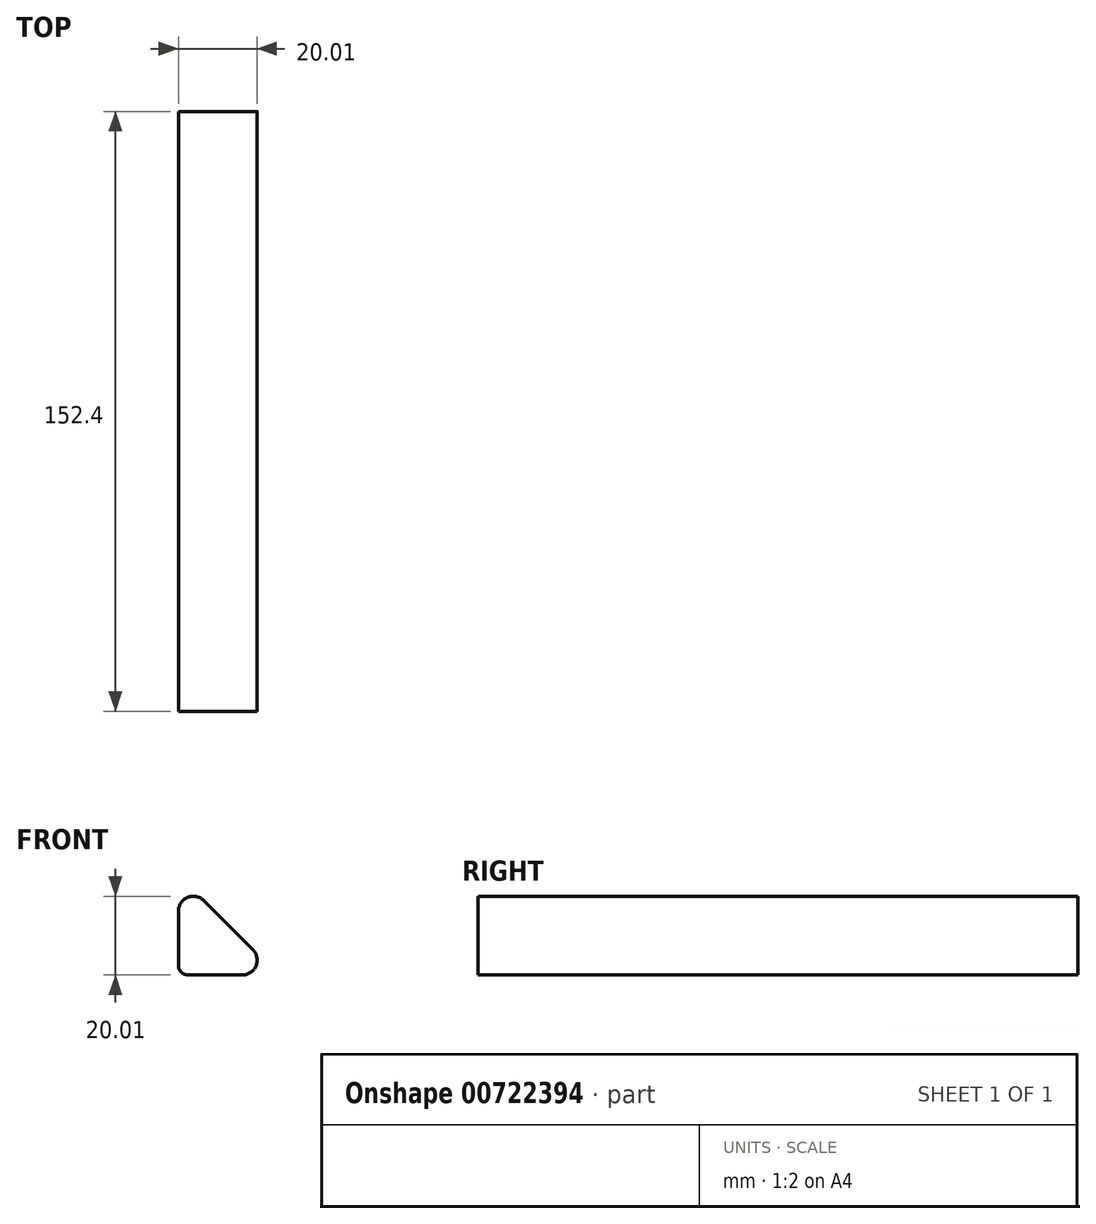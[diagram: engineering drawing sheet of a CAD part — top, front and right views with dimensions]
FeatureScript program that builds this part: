
annotation { "Feature Type Name" : "Feature", "Feature Type Description" : "" }
export const myFeature = defineFeature(function(context is Context, id is Id, definition is map)
    precondition{}
    {
        {
            var Q0;
            Q0=qCreatedBy(makeId("Front.planeOp"),FACE);
            var sketch = newSketch(context, id + "F0", { "sketchPlane" : qUnion([Q0])});
            skLineSegment(sketch, "E0", {"start": v(0, 0) * mm, "end": v(0, 25.4) * mm});
            skLineSegment(sketch, "E1", {"start": v(0, 25.4) * mm, "end": v(25.4, 0) * mm});
            skLineSegment(sketch, "E2", {"start": v(25.4, 0) * mm, "end": v(0, 0) * mm});
            skSolve(sketch);
        }
        {
            var Q0;
            Q0 = qSketchRegion(id + "F0", true);
            extrude(context, id + "F1", {"entities" : qUnion([Q0]), "depth" : 152.4 * mm, "offsetDistance" : 25.4 * mm});
        }
        {
            var Q0;
            Q0=makeQuery(id+"F1.opExtrude","SWEPT_EDGE",EDGE,{"disambiguationData":[OSD([sQuery(id+"F0.wireOp",EDGE,"E0"),sQuery(id+"F0.wireOp",EDGE,"E1")])]});
            var Q1;
            Q1=makeQuery(id+"F1.opExtrude","SWEPT_EDGE",EDGE,{"disambiguationData":[OSD([sQuery(id+"F0.wireOp",EDGE,"E1"),sQuery(id+"F0.wireOp",EDGE,"E2")])]});
            fillet(context, id + "F2", {"entities" : qUnion([Q0, Q1]), "radius" : 3.8 * mm, "tangentPropagation" : true, "allowEdgeOverflow" : false});
        }
        {
            var Q0;
            Q0=makeQuery(id+"F1.opExtrude","SWEPT_EDGE",EDGE,{"disambiguationData":[OSD([sQuery(id+"F0.wireOp",EDGE,"E0"),sQuery(id+"F0.wireOp",EDGE,"E2")])]});
            fillet(context, id + "F3", {"entities" : qUnion([Q0]), "radius" : 2.54 * mm, "tangentPropagation" : true, "allowEdgeOverflow" : false});
        }
    });
